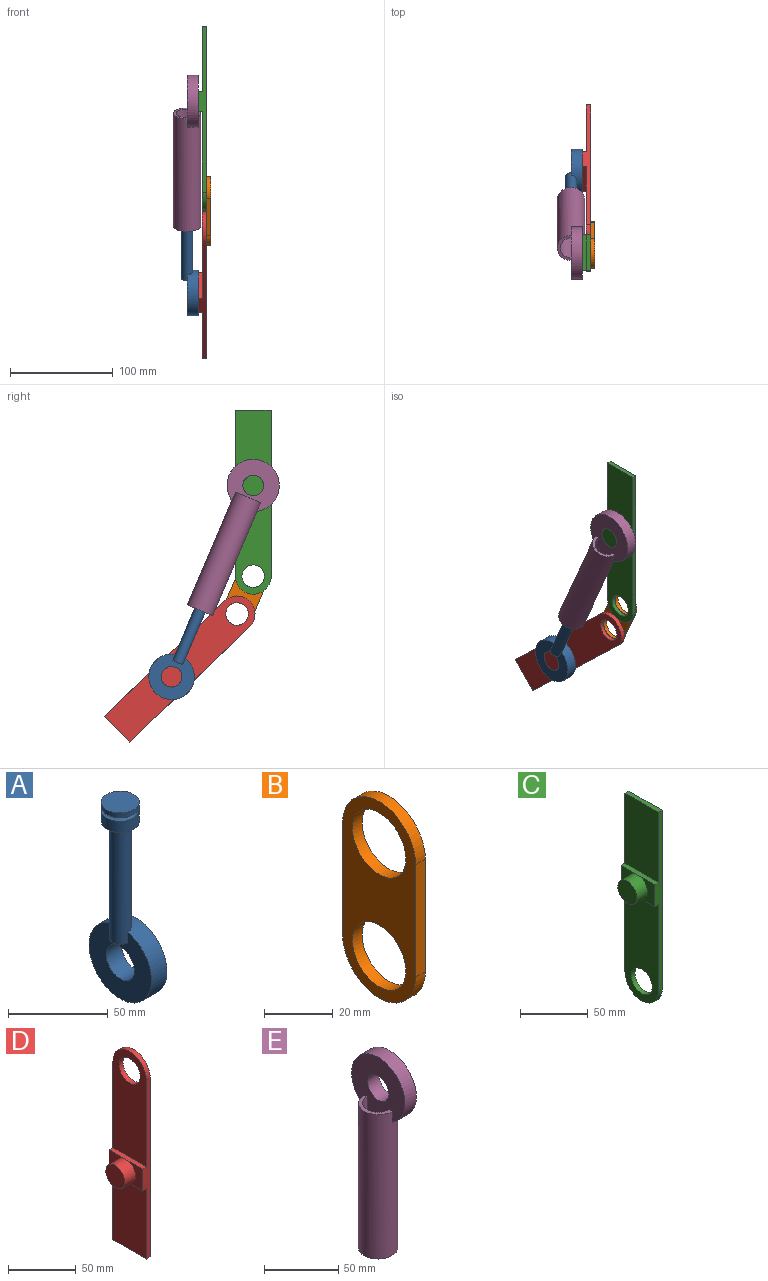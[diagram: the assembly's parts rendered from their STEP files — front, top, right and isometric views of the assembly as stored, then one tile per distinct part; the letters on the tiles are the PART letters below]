
ASSEMBLY  parts=5 mates=5
PART A: 11 faces, bbox 21.7x44.3x121 mm
  f0: plane 44.35x43.66mm, normal (-1,0,0), area 1155.6mm2, adj f1,f2,f4,f5
  f1: cylinder r=22.17mm len=44.35mm, axis (1,0,0), area 1484.7mm2, adj f0,f3,f5
  f2: cylinder r=10mm len=20mm, axis (1,0,0), area 691.2mm2, adj f0,f3
  f3: plane 44.35x44.35mm, normal (1,0,0), area 1230.4mm2, adj f1,f2
  f4: plane 10.99x5.49mm, normal (0,0,-1), area 47.4mm2, adj f0,f5
  f5: cylinder r=5.49mm len=71.59mm, axis (0,0,1), area 2355.6mm2, adj f0,f1,f4,f10
  f6: plane 19.12x19.12mm, normal (0,0,1), area 287.3mm2, adj f7
  f7: cylinder r=9.56mm len=19.12mm, axis (0,0,1), area 180.5mm2, adj f6,f8
  f8: torus R=7.67mm, axis (0,0,1), area 521mm2, adj f7,f9
  f9: cylinder r=9.56mm len=19.12mm, axis (0,0,1), area 415.2mm2, adj f8,f10
  f10: plane 19.12x19.12mm, normal (0,0,-1), area 192.4mm2, adj f5,f9
PART B: 8 faces, bbox 4x30x70 mm
  f0: plane 40x4mm, normal (0,1,0), area 160mm2, adj f1,f4,f6,f7
  f1: cylinder r=15mm len=30mm, axis (-1,0,0), area 188.5mm2, adj f0,f2,f6,f7
  f2: plane 40x4mm, normal (0,-1,0), area 160mm2, adj f1,f4,f6,f7
  f3: cylinder r=11mm len=22mm, axis (-1,0,0), area 276.5mm2, adj f6,f7
  f4: cylinder r=15mm len=30mm, axis (-1,0,0), area 188.5mm2, adj f0,f2,f6,f7
  f5: cylinder r=11mm len=22mm, axis (-1,0,0), area 276.5mm2, adj f6,f7
  f6: plane 70x30mm, normal (1,0,0), area 1146.6mm2, adj f0,f1,f2,f3,f4,f5
  f7: plane 70x30mm, normal (-1,0,0), area 1146.6mm2, adj f0,f1,f2,f3,f4,f5
PART C: 14 faces, bbox 19x35x179.3 mm
  f0: plane 95.83x35mm, normal (-1,0,0), area 2842.5mm2, adj f1,f2,f3,f5,f9
  f1: plane 161.82x8mm, normal (0,-1,0), area 727.3mm2, adj f0,f2,f4,f6,f7,f8,f9,f10
  f2: cylinder r=17.5mm len=35mm, axis (1,0,0), area 219.9mm2, adj f0,f1,f3,f7
  f3: plane 161.82x8mm, normal (0,1,0), area 727.3mm2, adj f0,f2,f4,f6,f7,f9,f10,f11
  f4: plane 35x4mm, normal (0,0,1), area 140mm2, adj f1,f3,f6,f7
  f5: cylinder r=11mm len=22mm, axis (1,0,0), area 276.5mm2, adj f0,f7
  f6: plane 63.49x35mm, normal (-1,0,0), area 2222mm2, adj f1,f3,f4,f10
  f7: plane 179.32x35mm, normal (1,0,0), area 5764.5mm2, adj f1,f2,f3,f4,f5
  f8: plane 20x17.5mm, normal (-1,0,0), area 192.9mm2, adj f1,f9,f10,f12
  f9: plane 35x4mm, normal (0,0,-1), area 140mm2, adj f0,f1,f3,f8,f11
  f10: plane 35x4mm, normal (0,0,1), area 140mm2, adj f1,f3,f6,f8,f11
  f11: plane 20x17.5mm, normal (-1,0,0), area 192.9mm2, adj f3,f9,f10,f12
  f12: cylinder r=10mm len=20mm, axis (1,0,0), area 691.2mm2, adj f8,f11,f13
  f13: plane 20x20mm, normal (-1,0,0), area 314.2mm2, adj f12
PART D: 14 faces, bbox 19x35x179.3 mm
  f0: plane 63.49x35mm, normal (-1,0,0), area 2222mm2, adj f2,f3,f5,f10
  f1: cylinder r=17.5mm len=35mm, axis (1,0,0), area 219.9mm2, adj f2,f5,f6,f7
  f2: plane 161.82x8mm, normal (0,-1,0), area 727.3mm2, adj f0,f1,f3,f6,f7,f8,f9,f10
  f3: plane 35x4mm, normal (0,0,-1), area 140mm2, adj f0,f2,f5,f7
  f4: cylinder r=11mm len=22mm, axis (1,0,0), area 276.5mm2, adj f6,f7
  f5: plane 161.82x8mm, normal (0,1,0), area 727.3mm2, adj f0,f1,f3,f6,f7,f9,f10,f11
  f6: plane 95.83x35mm, normal (-1,0,0), area 2842.5mm2, adj f1,f2,f4,f5,f9
  f7: plane 179.32x35mm, normal (1,0,0), area 5764.5mm2, adj f1,f2,f3,f4,f5
  f8: plane 20x17.5mm, normal (-1,0,0), area 192.9mm2, adj f2,f9,f10,f12
  f9: plane 35x4mm, normal (0,0,1), area 140mm2, adj f2,f5,f6,f8,f11
  f10: plane 35x4mm, normal (0,0,-1), area 140mm2, adj f0,f2,f5,f8,f11
  f11: plane 20x17.5mm, normal (-1,0,0), area 192.9mm2, adj f5,f9,f10,f12
  f12: cylinder r=10mm len=20mm, axis (1,0,0), area 691.2mm2, adj f8,f11,f13
  f13: plane 20x20mm, normal (-1,0,0), area 314.2mm2, adj f12
PART E: 10 faces, bbox 26.7x50.9x157.5 mm
  f0: cylinder r=25.44mm len=21.12mm, axis (1,0,0), area 179.3mm2, adj f4,f5
  f1: cylinder r=10mm len=20mm, axis (1,0,0), area 691.2mm2, adj f2,f4
  f2: plane 50.88x49.73mm, normal (1,0,0), area 1530.7mm2, adj f1,f3,f7,f8
  f3: cylinder r=25.44mm len=50.88mm, axis (1,0,0), area 1491.7mm2, adj f2,f4,f8
  f4: plane 50.88x50.88mm, normal (-1,0,0), area 1664.2mm2, adj f0,f1,f3,f5,f6,f8
  f5: cylinder r=10.56mm len=119.38mm, axis (0,0,1), area 7535.2mm2, adj f0,f4,f6,f9
  f6: plane 26.71x13.36mm, normal (0,0,1), area 105mm2, adj f4,f5,f8
  f7: plane 15.15x2.36mm, normal (0,0,1), area 24.3mm2, adj f2,f8
  f8: cylinder r=13.36mm len=119.38mm, axis (0,0,1), area 9759.1mm2, adj f2,f3,f4,f6,f7,f9
  f9: plane 26.71x26.71mm, normal (0,0,-1), area 210mm2, adj f5,f8
PLACE A rot(axis=(1,0,0),23.1deg) t=(-30,36.93,-77.19)mm
PLACE B rot(axis=(1,0,0),23.1deg) t=(-30,7.84,-97.27)mm
PLACE C t=(-30,0,-98.87)mm
PLACE D rot(axis=(1,0,0),46.2deg) t=(-30,1.26,-101.82)mm
PLACE E rot(axis=(1,0,0),23.1deg) t=(-30,42.47,-90.2)mm
MATE revolute C.f12 <-> E.f0  axis (-1,0,0) through (-8,0,9.46)mm
MATE revolute A.f1 <-> D.f12  axis (1,0,0) through (-8,79.4,-176.85)mm
MATE slider A.f5 <-> E.f5  axis (0,-0.39,0.92) through (-19,40.66,-85.95)mm
MATE revolute C.f5 <-> B.f1  axis (1,0,0) through (0,0,-78.87)mm
MATE revolute D.f4 <-> B.f3  axis (1,0,0) through (0,15.68,-115.67)mm
